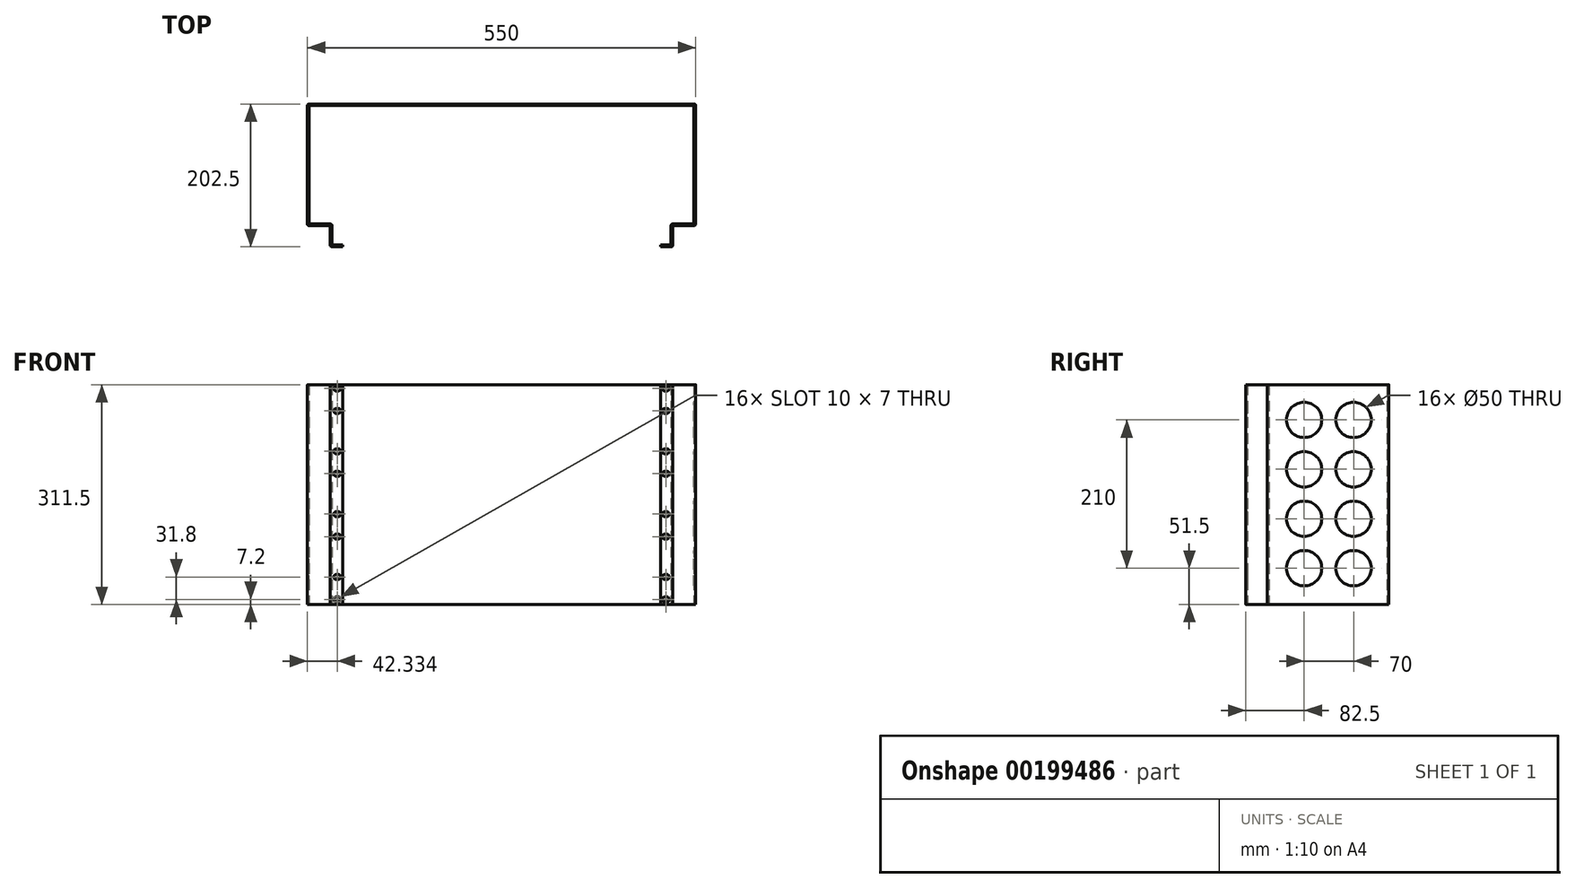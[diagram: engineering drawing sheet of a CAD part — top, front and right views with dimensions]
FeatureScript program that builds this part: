
annotation { "Feature Type Name" : "Feature", "Feature Type Description" : "" }
export const myFeature = defineFeature(function(context is Context, id is Id, definition is map)
    precondition{}
    {
        {
            var Q0;
            Q0=qCreatedBy(makeId("Front.planeOp"),FACE);
            var sketch = newSketch(context, id + "F0", { "sketchPlane" : qUnion([Q0])});
            skLineSegment(sketch, "E0.bottom", {"start": v(-275, 155.75) * mm, "end": v(0, 155.75) * mm});
            skLineSegment(sketch, "E0.top", {"start": v(-275, -155.75) * mm, "end": v(0, -155.75) * mm});
            skLineSegment(sketch, "E0.left", {"start": v(-275, 155.75) * mm, "end": v(-275, -155.75) * mm});
            skLineSegment(sketch, "E0.right", {"start": v(0, 155.75) * mm, "end": v(0, -155.75) * mm});
            skLineSegment(sketch, "E1", {"start": v(-272.5, 155.75) * mm, "end": v(-272.5, -155.75) * mm});
            skSolve(sketch);
        }
        {
            var Q0;
            {var subQ0=sQuery(id+"F0.wireOp",EDGE,"E0.left");Q0=makeQuery(id+"F0.imprint","IMPRINT",FACE,{"disambiguationData":[TD([[makeQuery(id+"F0.imprint","IMPRINT",EDGE,{"derivedFrom":subQ0}),1.0]])]});}
            extrude(context, id + "F1", {"entities" : qUnion([Q0]), "depth" : 170 * mm});
        }
        {
            var Q0;
            {var subQ0=sQuery(id+"F0.wireOp",EDGE,"E0.right");Q0=makeQuery(id+"F0.imprint","IMPRINT",FACE,{"disambiguationData":[TD([[makeQuery(id+"F0.imprint","IMPRINT",EDGE,{"derivedFrom":subQ0}),-1.0]])]});}
            var Q1;
            {var subQ0=sQuery(id+"F0.wireOp",EDGE,"E0.left");Q1=makeQuery(id+"F0.imprint","IMPRINT",FACE,{"disambiguationData":[TD([[makeQuery(id+"F0.imprint","IMPRINT",EDGE,{"derivedFrom":subQ0}),1.0]])]});}
            extrude(context, id + "F2", {"entities" : qUnion([Q0, Q1]), "operationType" : NewBodyOperationType.ADD, "oppositeDirection" : true, "depth" : 2.5 * mm});
        }
        {
            var Q0;
            Q0=makeQuery(id+"F1.opExtrude","SWEPT_FACE",FACE,{"disambiguationData":[OSD([sQuery(id+"F0.wireOp",EDGE,"E1")])]});
            var sketch = newSketch(context, id + "F3", { "sketchPlane" : qUnion([Q0])});
            skLineSegment(sketch, "E2", {"start": v(-167.5, 155.75) * mm, "end": v(-167.5, -155.75) * mm});
            skCircle(sketch, "E3", {"center": v(-117.5, 105.75) * mm, "radius": 25 * mm});
            skCircle(sketch, "E4.0.1.0", {"center": v(-117.5, 35.75) * mm, "radius": 25 * mm});
            skCircle(sketch, "E4.0.2.0", {"center": v(-117.5, -34.25) * mm, "radius": 25 * mm});
            skCircle(sketch, "E4.0.3.0", {"center": v(-117.5, -104.25) * mm, "radius": 25 * mm});
            skCircle(sketch, "E4.1.0.0", {"center": v(-47.5, 105.75) * mm, "radius": 25 * mm});
            skCircle(sketch, "E4.1.1.0", {"center": v(-47.5, 35.75) * mm, "radius": 25 * mm});
            skCircle(sketch, "E4.1.2.0", {"center": v(-47.5, -34.25) * mm, "radius": 25 * mm});
            skCircle(sketch, "E4.1.3.0", {"center": v(-47.5, -104.25) * mm, "radius": 25 * mm});
            skLineSegment(sketch, "E4.direction1", {"start": v(-117.5, 105.75) * mm, "end": v(-47.5, 105.75) * mm, "construction": true});
            skLineSegment(sketch, "E4.direction2", {"start": v(-117.5, 105.75) * mm, "end": v(-117.5, 35.75) * mm, "construction": true});
            skSolve(sketch);
        }
        {
            var Q0;
            {var subQ0=sQuery(id+"F3.wireOp",EDGE,"E2");Q0=makeQuery(id+"F3.imprint","IMPRINT",FACE,{"disambiguationData":[TD([[makeQuery(id+"F3.imprint","IMPRINT",EDGE,{"derivedFrom":subQ0}),-1.0]])]});}
            extrude(context, id + "F4", {"entities" : qUnion([Q0]), "operationType" : NewBodyOperationType.ADD, "depth" : 32.5 * mm});
        }
        {
            var Q0;
            {var subQ0=sQuery(id+"F0.wireOp",EDGE,"E1");Q0=makeQuery(id+"F4.boolean.opBoolean","MERGE",FACE,{"derivedFrom":[makeQuery(id+"F1.opExtrude","CAP_FACE",FACE,{"disambiguationData":[OSD([sQuery(id+"F0.wireOp",EDGE,"E0.bottom"),sQuery(id+"F0.wireOp",EDGE,"E0.top"),sQuery(id+"F0.wireOp",EDGE,"E0.left"),subQ0])],"isStart":false}),makeQuery(id+"F4.opExtrude","SWEPT_FACE",FACE,{"disambiguationData":[OSD([subQ0])]})]});}
            var sketch = newSketch(context, id + "F5", { "sketchPlane" : qUnion([Q0])});
            skLineSegment(sketch, "E5", {"start": v(-242.5, 155.75) * mm, "end": v(-242.5, -155.75) * mm});
            skSolve(sketch);
        }
        {
            var Q0;
            {var subQ0=sQuery(id+"F5.wireOp",EDGE,"E5");Q0=makeQuery(id+"F5.imprint","IMPRINT",FACE,{"disambiguationData":[TD([[makeQuery(id+"F5.imprint","IMPRINT",EDGE,{"derivedFrom":subQ0}),1.0]])]});}
            extrude(context, id + "F6", {"entities" : qUnion([Q0]), "operationType" : NewBodyOperationType.ADD, "depth" : 30 * mm});
        }
        {
            var Q0;
            {var subQ0=sQuery(id+"F0.wireOp",EDGE,"E1");Q0=makeQuery(id+"F6.boolean.opBoolean","MERGE",FACE,{"derivedFrom":[makeQuery(id+"F4.opExtrude","CAP_FACE",FACE,{"disambiguationData":[OSD([sQuery(id+"F0.wireOp",EDGE,"E0.bottom"),sQuery(id+"F0.wireOp",EDGE,"E0.top"),subQ0,sQuery(id+"F3.wireOp",EDGE,"E2")])],"isStart":false}),makeQuery(id+"F6.opExtrude","SWEPT_FACE",FACE,{"disambiguationData":[OSD([subQ0])]})]});}
            var sketch = newSketch(context, id + "F7", { "sketchPlane" : qUnion([Q0])});
            skLineSegment(sketch, "E6", {"start": v(-197.5, 155.75) * mm, "end": v(-197.5, -155.75) * mm});
            skSolve(sketch);
        }
        {
            var Q0;
            {var subQ0=sQuery(id+"F7.wireOp",EDGE,"E6");Q0=makeQuery(id+"F7.imprint","IMPRINT",FACE,{"disambiguationData":[TD([[makeQuery(id+"F7.imprint","IMPRINT",EDGE,{"derivedFrom":subQ0}),-1.0]])]});}
            extrude(context, id + "F8", {"entities" : qUnion([Q0]), "operationType" : NewBodyOperationType.ADD, "depth" : 15 * mm});
        }
        {
            var Q0;
            Q0=makeQuery(id+"F3.imprint","IMPRINT",FACE,{"disambiguationData":[TD([[makeQuery(id+"F3.imprint","IMPRINT",EDGE,{"derivedFrom":sQuery(id+"F3.wireOp",EDGE,"E3")}),1.0]])]});
            var Q1;
            Q1=makeQuery(id+"F3.imprint","IMPRINT",FACE,{"disambiguationData":[TD([[makeQuery(id+"F3.imprint","IMPRINT",EDGE,{"derivedFrom":sQuery(id+"F3.wireOp",EDGE,"E4.1.0.0")}),1.0]])]});
            var Q2;
            Q2=makeQuery(id+"F3.imprint","IMPRINT",FACE,{"disambiguationData":[TD([[makeQuery(id+"F3.imprint","IMPRINT",EDGE,{"derivedFrom":sQuery(id+"F3.wireOp",EDGE,"E4.0.1.0")}),1.0]])]});
            var Q3;
            Q3=makeQuery(id+"F3.imprint","IMPRINT",FACE,{"disambiguationData":[TD([[makeQuery(id+"F3.imprint","IMPRINT",EDGE,{"derivedFrom":sQuery(id+"F3.wireOp",EDGE,"E4.1.1.0")}),1.0]])]});
            var Q4;
            Q4=makeQuery(id+"F3.imprint","IMPRINT",FACE,{"disambiguationData":[TD([[makeQuery(id+"F3.imprint","IMPRINT",EDGE,{"derivedFrom":sQuery(id+"F3.wireOp",EDGE,"E4.0.2.0")}),1.0]])]});
            var Q5;
            Q5=makeQuery(id+"F3.imprint","IMPRINT",FACE,{"disambiguationData":[TD([[makeQuery(id+"F3.imprint","IMPRINT",EDGE,{"derivedFrom":sQuery(id+"F3.wireOp",EDGE,"E4.1.2.0")}),1.0]])]});
            var Q6;
            Q6=makeQuery(id+"F3.imprint","IMPRINT",FACE,{"disambiguationData":[TD([[makeQuery(id+"F3.imprint","IMPRINT",EDGE,{"derivedFrom":sQuery(id+"F3.wireOp",EDGE,"E4.1.3.0")}),1.0]])]});
            var Q7;
            Q7=makeQuery(id+"F3.imprint","IMPRINT",FACE,{"disambiguationData":[TD([[makeQuery(id+"F3.imprint","IMPRINT",EDGE,{"derivedFrom":sQuery(id+"F3.wireOp",EDGE,"E4.0.3.0")}),1.0]])]});
            extrude(context, id + "F9", {"entities" : qUnion([Q0, Q1, Q2, Q3, Q4, Q5, Q6, Q7]), "operationType" : NewBodyOperationType.REMOVE, "oppositeDirection" : true, "depth" : 25 * mm});
        }
        {
            var Q0;
            {var subQ0=sQuery(id+"F0.wireOp",EDGE,"E1");Q0=makeQuery(id+"F8.boolean.opBoolean","MERGE",FACE,{"derivedFrom":[makeQuery(id+"F6.opExtrude","CAP_FACE",FACE,{"disambiguationData":[OSD([sQuery(id+"F0.wireOp",EDGE,"E0.bottom"),sQuery(id+"F0.wireOp",EDGE,"E0.top"),subQ0,sQuery(id+"F5.wireOp",EDGE,"E5")])],"isStart":false}),makeQuery(id+"F8.opExtrude","SWEPT_FACE",FACE,{"disambiguationData":[OSD([subQ0])]})]});}
            var sketch = newSketch(context, id + "F10", { "sketchPlane" : qUnion([Q0])});
            skLineSegment(sketch, "E7.bottom", {"start": v(-234.17, 153.75) * mm, "end": v(-231.17, 153.75) * mm});
            skLineSegment(sketch, "E7.top", {"start": v(-234.17, 146.75) * mm, "end": v(-231.17, 146.75) * mm});
            skArc(sketch, "E8", {"start": v(-234.17, 153.75) * mm, "mid": v(-237.67, 150.25) * mm, "end": v(-234.17, 146.75) * mm});
            skArc(sketch, "E9", {"start": v(-231.17, 146.75) * mm, "mid": v(-227.67, 150.25) * mm, "end": v(-231.17, 153.75) * mm});
            skLineSegment(sketch, "E10.0.1.0", {"start": v(-234.17, 121.95) * mm, "end": v(-231.17, 121.95) * mm});
            skArc(sketch, "E10.0.1.1", {"start": v(-231.17, 114.95) * mm, "mid": v(-227.67, 118.45) * mm, "end": v(-231.17, 121.95) * mm});
            skLineSegment(sketch, "E10.0.1.2", {"start": v(-234.17, 114.95) * mm, "end": v(-231.17, 114.95) * mm});
            skArc(sketch, "E10.0.1.3", {"start": v(-234.17, 121.95) * mm, "mid": v(-237.67, 118.45) * mm, "end": v(-234.17, 114.95) * mm});
            skLineSegment(sketch, "E10.direction2", {"start": v(-234.17, 146.75) * mm, "end": v(-234.17, 114.95) * mm, "construction": true});
            skArc(sketch, "E11.0.1.0", {"start": v(-231.17, 25.95) * mm, "mid": v(-227.67, 29.45) * mm, "end": v(-231.17, 32.95) * mm});
            skLineSegment(sketch, "E11.0.1.1", {"start": v(-234.17, 25.95) * mm, "end": v(-231.17, 25.95) * mm});
            skArc(sketch, "E11.0.1.2", {"start": v(-231.17, 57.75) * mm, "mid": v(-227.67, 61.25) * mm, "end": v(-231.17, 64.75) * mm});
            skLineSegment(sketch, "E11.0.1.3", {"start": v(-234.17, 57.75) * mm, "end": v(-234.17, 25.95) * mm, "construction": true});
            skLineSegment(sketch, "E11.0.1.4", {"start": v(-234.17, 64.75) * mm, "end": v(-231.17, 64.75) * mm});
            skArc(sketch, "E11.0.1.5", {"start": v(-234.17, 32.95) * mm, "mid": v(-237.67, 29.45) * mm, "end": v(-234.17, 25.95) * mm});
            skLineSegment(sketch, "E11.0.1.6", {"start": v(-234.17, 57.75) * mm, "end": v(-231.17, 57.75) * mm});
            skArc(sketch, "E11.0.1.7", {"start": v(-234.17, 64.75) * mm, "mid": v(-237.67, 61.25) * mm, "end": v(-234.17, 57.75) * mm});
            skLineSegment(sketch, "E11.0.1.8", {"start": v(-234.17, 32.95) * mm, "end": v(-231.17, 32.95) * mm});
            skArc(sketch, "E11.0.2.0", {"start": v(-231.17, -63.05) * mm, "mid": v(-227.67, -59.55) * mm, "end": v(-231.17, -56.05) * mm});
            skLineSegment(sketch, "E11.0.2.1", {"start": v(-234.17, -63.05) * mm, "end": v(-231.17, -63.05) * mm});
            skArc(sketch, "E11.0.2.2", {"start": v(-231.17, -31.25) * mm, "mid": v(-227.67, -27.75) * mm, "end": v(-231.17, -24.25) * mm});
            skLineSegment(sketch, "E11.0.2.3", {"start": v(-234.17, -31.25) * mm, "end": v(-234.17, -63.05) * mm, "construction": true});
            skLineSegment(sketch, "E11.0.2.4", {"start": v(-234.17, -24.25) * mm, "end": v(-231.17, -24.25) * mm});
            skArc(sketch, "E11.0.2.5", {"start": v(-234.17, -56.05) * mm, "mid": v(-237.67, -59.55) * mm, "end": v(-234.17, -63.05) * mm});
            skLineSegment(sketch, "E11.0.2.6", {"start": v(-234.17, -31.25) * mm, "end": v(-231.17, -31.25) * mm});
            skArc(sketch, "E11.0.2.7", {"start": v(-234.17, -24.25) * mm, "mid": v(-237.67, -27.75) * mm, "end": v(-234.17, -31.25) * mm});
            skLineSegment(sketch, "E11.0.2.8", {"start": v(-234.17, -56.05) * mm, "end": v(-231.17, -56.05) * mm});
            skArc(sketch, "E11.0.3.0", {"start": v(-231.17, -152.05) * mm, "mid": v(-227.67, -148.55) * mm, "end": v(-231.17, -145.05) * mm});
            skLineSegment(sketch, "E11.0.3.1", {"start": v(-234.17, -152.05) * mm, "end": v(-231.17, -152.05) * mm});
            skArc(sketch, "E11.0.3.2", {"start": v(-231.17, -120.25) * mm, "mid": v(-227.67, -116.75) * mm, "end": v(-231.17, -113.25) * mm});
            skLineSegment(sketch, "E11.0.3.3", {"start": v(-234.17, -120.25) * mm, "end": v(-234.17, -152.05) * mm, "construction": true});
            skLineSegment(sketch, "E11.0.3.4", {"start": v(-234.17, -113.25) * mm, "end": v(-231.17, -113.25) * mm});
            skArc(sketch, "E11.0.3.5", {"start": v(-234.17, -145.05) * mm, "mid": v(-237.67, -148.55) * mm, "end": v(-234.17, -152.05) * mm});
            skLineSegment(sketch, "E11.0.3.6", {"start": v(-234.17, -120.25) * mm, "end": v(-231.17, -120.25) * mm});
            skArc(sketch, "E11.0.3.7", {"start": v(-234.17, -113.25) * mm, "mid": v(-237.67, -116.75) * mm, "end": v(-234.17, -120.25) * mm});
            skLineSegment(sketch, "E11.0.3.8", {"start": v(-234.17, -145.05) * mm, "end": v(-231.17, -145.05) * mm});
            skArc(sketch, "E11.1.0.0", {"start": v(-206.17, 114.95) * mm, "mid": v(-202.67, 118.45) * mm, "end": v(-206.17, 121.95) * mm});
            skLineSegment(sketch, "E11.1.0.1", {"start": v(-209.17, 114.95) * mm, "end": v(-206.17, 114.95) * mm});
            skArc(sketch, "E11.1.0.2", {"start": v(-206.17, 146.75) * mm, "mid": v(-202.67, 150.25) * mm, "end": v(-206.17, 153.75) * mm});
            skLineSegment(sketch, "E11.1.0.3", {"start": v(-209.17, 146.75) * mm, "end": v(-209.17, 114.95) * mm, "construction": true});
            skLineSegment(sketch, "E11.1.0.4", {"start": v(-209.17, 153.75) * mm, "end": v(-206.17, 153.75) * mm});
            skArc(sketch, "E11.1.0.5", {"start": v(-209.17, 121.95) * mm, "mid": v(-212.67, 118.45) * mm, "end": v(-209.17, 114.95) * mm});
            skLineSegment(sketch, "E11.1.0.6", {"start": v(-209.17, 146.75) * mm, "end": v(-206.17, 146.75) * mm});
            skArc(sketch, "E11.1.0.7", {"start": v(-209.17, 153.75) * mm, "mid": v(-212.67, 150.25) * mm, "end": v(-209.17, 146.75) * mm});
            skLineSegment(sketch, "E11.1.0.8", {"start": v(-209.17, 121.95) * mm, "end": v(-206.17, 121.95) * mm});
            skArc(sketch, "E11.1.1.0", {"start": v(-206.17, 25.95) * mm, "mid": v(-202.67, 29.45) * mm, "end": v(-206.17, 32.95) * mm});
            skLineSegment(sketch, "E11.1.1.1", {"start": v(-209.17, 25.95) * mm, "end": v(-206.17, 25.95) * mm});
            skArc(sketch, "E11.1.1.2", {"start": v(-206.17, 57.75) * mm, "mid": v(-202.67, 61.25) * mm, "end": v(-206.17, 64.75) * mm});
            skLineSegment(sketch, "E11.1.1.3", {"start": v(-209.17, 57.75) * mm, "end": v(-209.17, 25.95) * mm, "construction": true});
            skLineSegment(sketch, "E11.1.1.4", {"start": v(-209.17, 64.75) * mm, "end": v(-206.17, 64.75) * mm});
            skArc(sketch, "E11.1.1.5", {"start": v(-209.17, 32.95) * mm, "mid": v(-212.67, 29.45) * mm, "end": v(-209.17, 25.95) * mm});
            skLineSegment(sketch, "E11.1.1.6", {"start": v(-209.17, 57.75) * mm, "end": v(-206.17, 57.75) * mm});
            skArc(sketch, "E11.1.1.7", {"start": v(-209.17, 64.75) * mm, "mid": v(-212.67, 61.25) * mm, "end": v(-209.17, 57.75) * mm});
            skLineSegment(sketch, "E11.1.1.8", {"start": v(-209.17, 32.95) * mm, "end": v(-206.17, 32.95) * mm});
            skArc(sketch, "E11.1.2.0", {"start": v(-206.17, -63.05) * mm, "mid": v(-202.67, -59.55) * mm, "end": v(-206.17, -56.05) * mm});
            skLineSegment(sketch, "E11.1.2.1", {"start": v(-209.17, -63.05) * mm, "end": v(-206.17, -63.05) * mm});
            skArc(sketch, "E11.1.2.2", {"start": v(-206.17, -31.25) * mm, "mid": v(-202.67, -27.75) * mm, "end": v(-206.17, -24.25) * mm});
            skLineSegment(sketch, "E11.1.2.3", {"start": v(-209.17, -31.25) * mm, "end": v(-209.17, -63.05) * mm, "construction": true});
            skLineSegment(sketch, "E11.1.2.4", {"start": v(-209.17, -24.25) * mm, "end": v(-206.17, -24.25) * mm});
            skArc(sketch, "E11.1.2.5", {"start": v(-209.17, -56.05) * mm, "mid": v(-212.67, -59.55) * mm, "end": v(-209.17, -63.05) * mm});
            skLineSegment(sketch, "E11.1.2.6", {"start": v(-209.17, -31.25) * mm, "end": v(-206.17, -31.25) * mm});
            skArc(sketch, "E11.1.2.7", {"start": v(-209.17, -24.25) * mm, "mid": v(-212.67, -27.75) * mm, "end": v(-209.17, -31.25) * mm});
            skLineSegment(sketch, "E11.1.2.8", {"start": v(-209.17, -56.05) * mm, "end": v(-206.17, -56.05) * mm});
            skArc(sketch, "E11.1.3.0", {"start": v(-206.17, -152.05) * mm, "mid": v(-202.67, -148.55) * mm, "end": v(-206.17, -145.05) * mm});
            skLineSegment(sketch, "E11.1.3.1", {"start": v(-209.17, -152.05) * mm, "end": v(-206.17, -152.05) * mm});
            skArc(sketch, "E11.1.3.2", {"start": v(-206.17, -120.25) * mm, "mid": v(-202.67, -116.75) * mm, "end": v(-206.17, -113.25) * mm});
            skLineSegment(sketch, "E11.1.3.3", {"start": v(-209.17, -120.25) * mm, "end": v(-209.17, -152.05) * mm, "construction": true});
            skLineSegment(sketch, "E11.1.3.4", {"start": v(-209.17, -113.25) * mm, "end": v(-206.17, -113.25) * mm});
            skArc(sketch, "E11.1.3.5", {"start": v(-209.17, -145.05) * mm, "mid": v(-212.67, -148.55) * mm, "end": v(-209.17, -152.05) * mm});
            skLineSegment(sketch, "E11.1.3.6", {"start": v(-209.17, -120.25) * mm, "end": v(-206.17, -120.25) * mm});
            skArc(sketch, "E11.1.3.7", {"start": v(-209.17, -113.25) * mm, "mid": v(-212.67, -116.75) * mm, "end": v(-209.17, -120.25) * mm});
            skLineSegment(sketch, "E11.1.3.8", {"start": v(-209.17, -145.05) * mm, "end": v(-206.17, -145.05) * mm});
            skArc(sketch, "E11.2.0.0", {"start": v(-181.17, 114.95) * mm, "mid": v(-177.67, 118.45) * mm, "end": v(-181.17, 121.95) * mm});
            skLineSegment(sketch, "E11.2.0.1", {"start": v(-184.17, 114.95) * mm, "end": v(-181.17, 114.95) * mm});
            skArc(sketch, "E11.2.0.2", {"start": v(-181.17, 146.75) * mm, "mid": v(-177.67, 150.25) * mm, "end": v(-181.17, 153.75) * mm});
            skLineSegment(sketch, "E11.2.0.3", {"start": v(-184.17, 146.75) * mm, "end": v(-184.17, 114.95) * mm, "construction": true});
            skLineSegment(sketch, "E11.2.0.4", {"start": v(-184.17, 153.75) * mm, "end": v(-181.17, 153.75) * mm});
            skArc(sketch, "E11.2.0.5", {"start": v(-184.17, 121.95) * mm, "mid": v(-187.67, 118.45) * mm, "end": v(-184.17, 114.95) * mm});
            skLineSegment(sketch, "E11.2.0.6", {"start": v(-184.17, 146.75) * mm, "end": v(-181.17, 146.75) * mm});
            skArc(sketch, "E11.2.0.7", {"start": v(-184.17, 153.75) * mm, "mid": v(-187.67, 150.25) * mm, "end": v(-184.17, 146.75) * mm});
            skLineSegment(sketch, "E11.2.0.8", {"start": v(-184.17, 121.95) * mm, "end": v(-181.17, 121.95) * mm});
            skArc(sketch, "E11.2.1.0", {"start": v(-181.17, 25.95) * mm, "mid": v(-177.67, 29.45) * mm, "end": v(-181.17, 32.95) * mm});
            skLineSegment(sketch, "E11.2.1.1", {"start": v(-184.17, 25.95) * mm, "end": v(-181.17, 25.95) * mm});
            skArc(sketch, "E11.2.1.2", {"start": v(-181.17, 57.75) * mm, "mid": v(-177.67, 61.25) * mm, "end": v(-181.17, 64.75) * mm});
            skLineSegment(sketch, "E11.2.1.3", {"start": v(-184.17, 57.75) * mm, "end": v(-184.17, 25.95) * mm, "construction": true});
            skLineSegment(sketch, "E11.2.1.4", {"start": v(-184.17, 64.75) * mm, "end": v(-181.17, 64.75) * mm});
            skArc(sketch, "E11.2.1.5", {"start": v(-184.17, 32.95) * mm, "mid": v(-187.67, 29.45) * mm, "end": v(-184.17, 25.95) * mm});
            skLineSegment(sketch, "E11.2.1.6", {"start": v(-184.17, 57.75) * mm, "end": v(-181.17, 57.75) * mm});
            skArc(sketch, "E11.2.1.7", {"start": v(-184.17, 64.75) * mm, "mid": v(-187.67, 61.25) * mm, "end": v(-184.17, 57.75) * mm});
            skLineSegment(sketch, "E11.2.1.8", {"start": v(-184.17, 32.95) * mm, "end": v(-181.17, 32.95) * mm});
            skArc(sketch, "E11.2.2.0", {"start": v(-181.17, -63.05) * mm, "mid": v(-177.67, -59.55) * mm, "end": v(-181.17, -56.05) * mm});
            skLineSegment(sketch, "E11.2.2.1", {"start": v(-184.17, -63.05) * mm, "end": v(-181.17, -63.05) * mm});
            skArc(sketch, "E11.2.2.2", {"start": v(-181.17, -31.25) * mm, "mid": v(-177.67, -27.75) * mm, "end": v(-181.17, -24.25) * mm});
            skLineSegment(sketch, "E11.2.2.3", {"start": v(-184.17, -31.25) * mm, "end": v(-184.17, -63.05) * mm, "construction": true});
            skLineSegment(sketch, "E11.2.2.4", {"start": v(-184.17, -24.25) * mm, "end": v(-181.17, -24.25) * mm});
            skArc(sketch, "E11.2.2.5", {"start": v(-184.17, -56.05) * mm, "mid": v(-187.67, -59.55) * mm, "end": v(-184.17, -63.05) * mm});
            skLineSegment(sketch, "E11.2.2.6", {"start": v(-184.17, -31.25) * mm, "end": v(-181.17, -31.25) * mm});
            skArc(sketch, "E11.2.2.7", {"start": v(-184.17, -24.25) * mm, "mid": v(-187.67, -27.75) * mm, "end": v(-184.17, -31.25) * mm});
            skLineSegment(sketch, "E11.2.2.8", {"start": v(-184.17, -56.05) * mm, "end": v(-181.17, -56.05) * mm});
            skArc(sketch, "E11.2.3.0", {"start": v(-181.17, -152.05) * mm, "mid": v(-177.67, -148.55) * mm, "end": v(-181.17, -145.05) * mm});
            skLineSegment(sketch, "E11.2.3.1", {"start": v(-184.17, -152.05) * mm, "end": v(-181.17, -152.05) * mm});
            skArc(sketch, "E11.2.3.2", {"start": v(-181.17, -120.25) * mm, "mid": v(-177.67, -116.75) * mm, "end": v(-181.17, -113.25) * mm});
            skLineSegment(sketch, "E11.2.3.3", {"start": v(-184.17, -120.25) * mm, "end": v(-184.17, -152.05) * mm, "construction": true});
            skLineSegment(sketch, "E11.2.3.4", {"start": v(-184.17, -113.25) * mm, "end": v(-181.17, -113.25) * mm});
            skArc(sketch, "E11.2.3.5", {"start": v(-184.17, -145.05) * mm, "mid": v(-187.67, -148.55) * mm, "end": v(-184.17, -152.05) * mm});
            skLineSegment(sketch, "E11.2.3.6", {"start": v(-184.17, -120.25) * mm, "end": v(-181.17, -120.25) * mm});
            skArc(sketch, "E11.2.3.7", {"start": v(-184.17, -113.25) * mm, "mid": v(-187.67, -116.75) * mm, "end": v(-184.17, -120.25) * mm});
            skLineSegment(sketch, "E11.2.3.8", {"start": v(-184.17, -145.05) * mm, "end": v(-181.17, -145.05) * mm});
            skLineSegment(sketch, "E11.direction1", {"start": v(-234.17, 114.95) * mm, "end": v(-209.17, 114.95) * mm, "construction": true});
            skLineSegment(sketch, "E11.direction2", {"start": v(-234.17, 114.95) * mm, "end": v(-234.17, 25.95) * mm, "construction": true});
            skSolve(sketch);
        }
        {
            var Q0;
            Q0 = qSketchRegion(id + "F10", true);
            extrude(context, id + "F11", {"entities" : qUnion([Q0]), "operationType" : NewBodyOperationType.REMOVE, "oppositeDirection" : true, "depth" : 25 * mm});
        }
        {
            var Q0;
            Q0=makeQuery(id+"F6.opExtrude","CAP_EDGE",EDGE,{"disambiguationData":[OSD([sQuery(id+"F5.wireOp",EDGE,"E5")])],"isStart":false});
            var Q1;
            Q1=makeQuery(id+"F6.opExtrude","CAP_EDGE",EDGE,{"disambiguationData":[OSD([sQuery(id+"F5.wireOp",EDGE,"E5")])],"isStart":true});
            var Q2;
            Q2=makeQuery(id+"F1.opExtrude","CAP_EDGE",EDGE,{"disambiguationData":[OSD([sQuery(id+"F0.wireOp",EDGE,"E0.left")])],"isStart":false});
            var Q3;
            Q3=makeQuery(id+"F4.opExtrude","CAP_EDGE",EDGE,{"disambiguationData":[OSD([sQuery(id+"F3.wireOp",EDGE,"E2")])],"isStart":false});
            var Q4;
            Q4=makeQuery(id+"F4.opExtrude","CAP_EDGE",EDGE,{"disambiguationData":[OSD([sQuery(id+"F3.wireOp",EDGE,"E2")])],"isStart":true});
            var Q5;
            Q5=makeQuery(id+"F8.opExtrude","CAP_EDGE",EDGE,{"disambiguationData":[OSD([sQuery(id+"F7.wireOp",EDGE,"E6")])],"isStart":true});
            var Q6;
            Q6=makeQuery(id+"F2.opExtrude","CAP_EDGE",EDGE,{"disambiguationData":[OSD([sQuery(id+"F0.wireOp",EDGE,"E0.left")])],"isStart":false});
            var Q7;
            Q7=makeQuery(id+"F1.opExtrude","CAP_EDGE",EDGE,{"disambiguationData":[OSD([sQuery(id+"F0.wireOp",EDGE,"E1")])],"isStart":true});
            fillet(context, id + "F12", {"entities" : qUnion([Q0, Q1, Q2, Q3, Q4, Q5, Q6, Q7]), "radius" : 2.5 * mm, "tangentPropagation" : true, "allowEdgeOverflow" : false});
        }
        {
            var Q0;
            Q0=makeQuery(id+"F1.opExtrude","SWEPT_BODY",BODY,{"disambiguationData":[OSD([sQuery(id+"F0.wireOp",EDGE,"E0.bottom"),sQuery(id+"F0.wireOp",EDGE,"E0.top"),sQuery(id+"F0.wireOp",EDGE,"E0.left"),sQuery(id+"F0.wireOp",EDGE,"E1")])]});
            var Q1;
            Q1=makeQuery(id+"F2.opExtrude","SWEPT_FACE",FACE,{"disambiguationData":[OSD([sQuery(id+"F0.wireOp",EDGE,"E0.right")])]});
            mirror(context, id + "F13", {"operationType" : NewBodyOperationType.ADD, "entities" : qUnion([Q0]), "mirrorPlane" : qUnion([Q1])});
        }
    });
